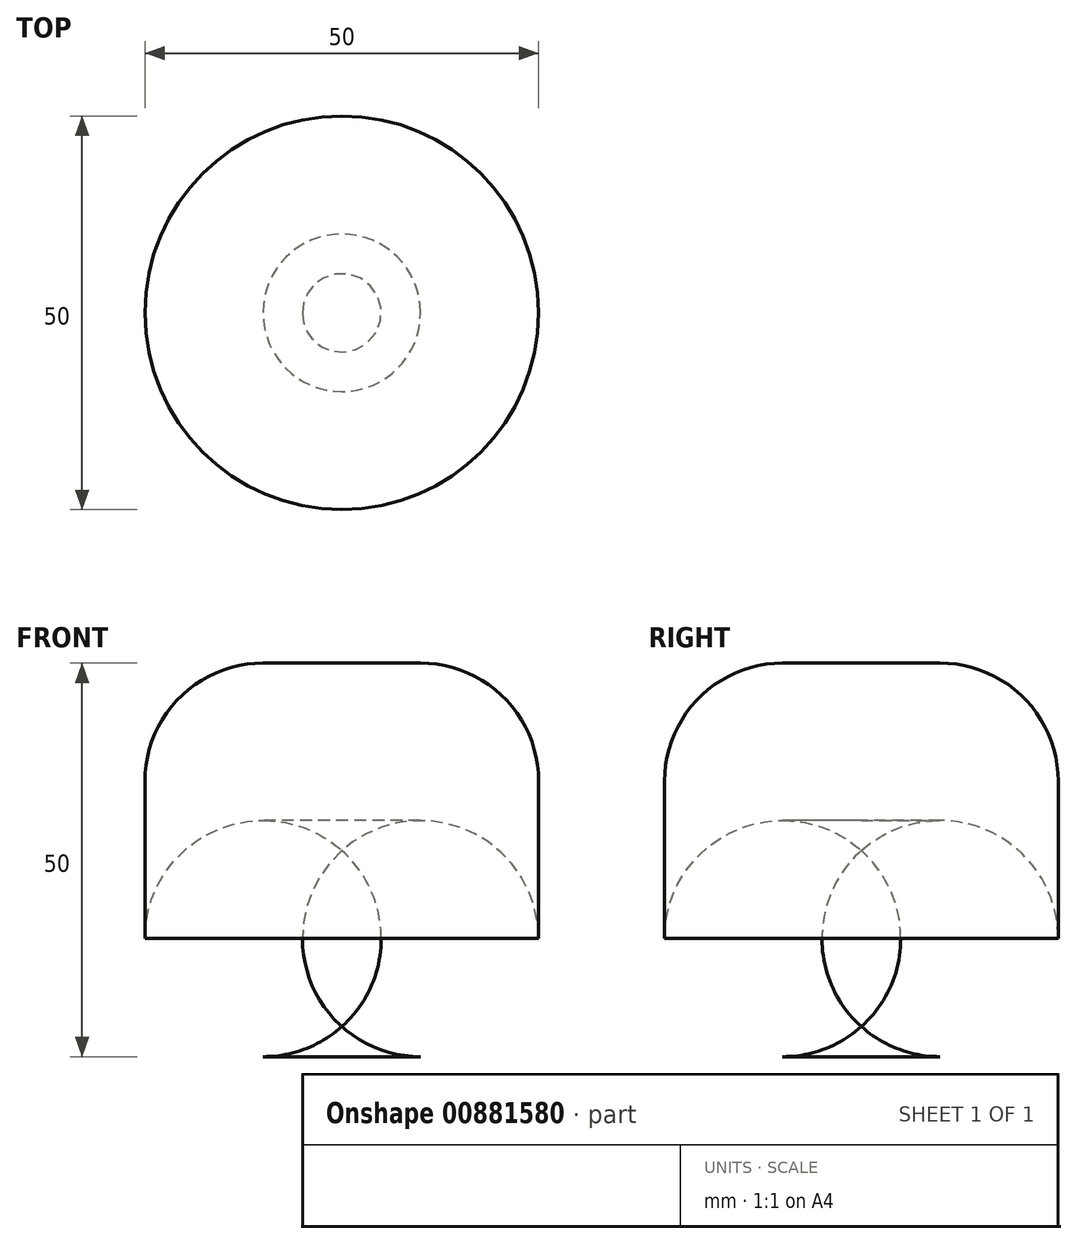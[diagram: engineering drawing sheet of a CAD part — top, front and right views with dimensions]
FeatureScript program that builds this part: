
annotation { "Feature Type Name" : "Feature", "Feature Type Description" : "" }
export const myFeature = defineFeature(function(context is Context, id is Id, definition is map)
    precondition{}
    {
        {
            var Q0;
            Q0=qCreatedBy(makeId("Top.planeOp"),FACE);
            var sketch = newSketch(context, id + "F0", { "sketchPlane" : qUnion([Q0])});
            skCircle(sketch, "E0", {"center": v(0, 0) * mm, "radius": 25 * mm});
            skSolve(sketch);
        }
        {
            var Q0;
            Q0=qSketchRegion(id+"F0",true);
            extrude(context, id + "F1", {"entities" : qUnion([Q0]), "depth" : 50 * mm, "offsetDistance" : 25 * mm});
        }
        {
            var Q0;
            Q0=makeQuery(id+"F1.opExtrude","CAP_FACE",FACE,{"disambiguationData":[OSD([sQuery(id+"F0.wireOp",EDGE,"E0")])],"isStart":false});
            var Q1;
            Q1=makeQuery(id+"F1.opExtrude","CAP_FACE",FACE,{"disambiguationData":[OSD([sQuery(id+"F0.wireOp",EDGE,"E0")])],"isStart":true});
            fillet(context, id + "F2", {"entities" : qUnion([Q0, Q1]), "radius" : 15 * mm, "tangentPropagation" : true, "allowEdgeOverflow" : false});
        }
    });
